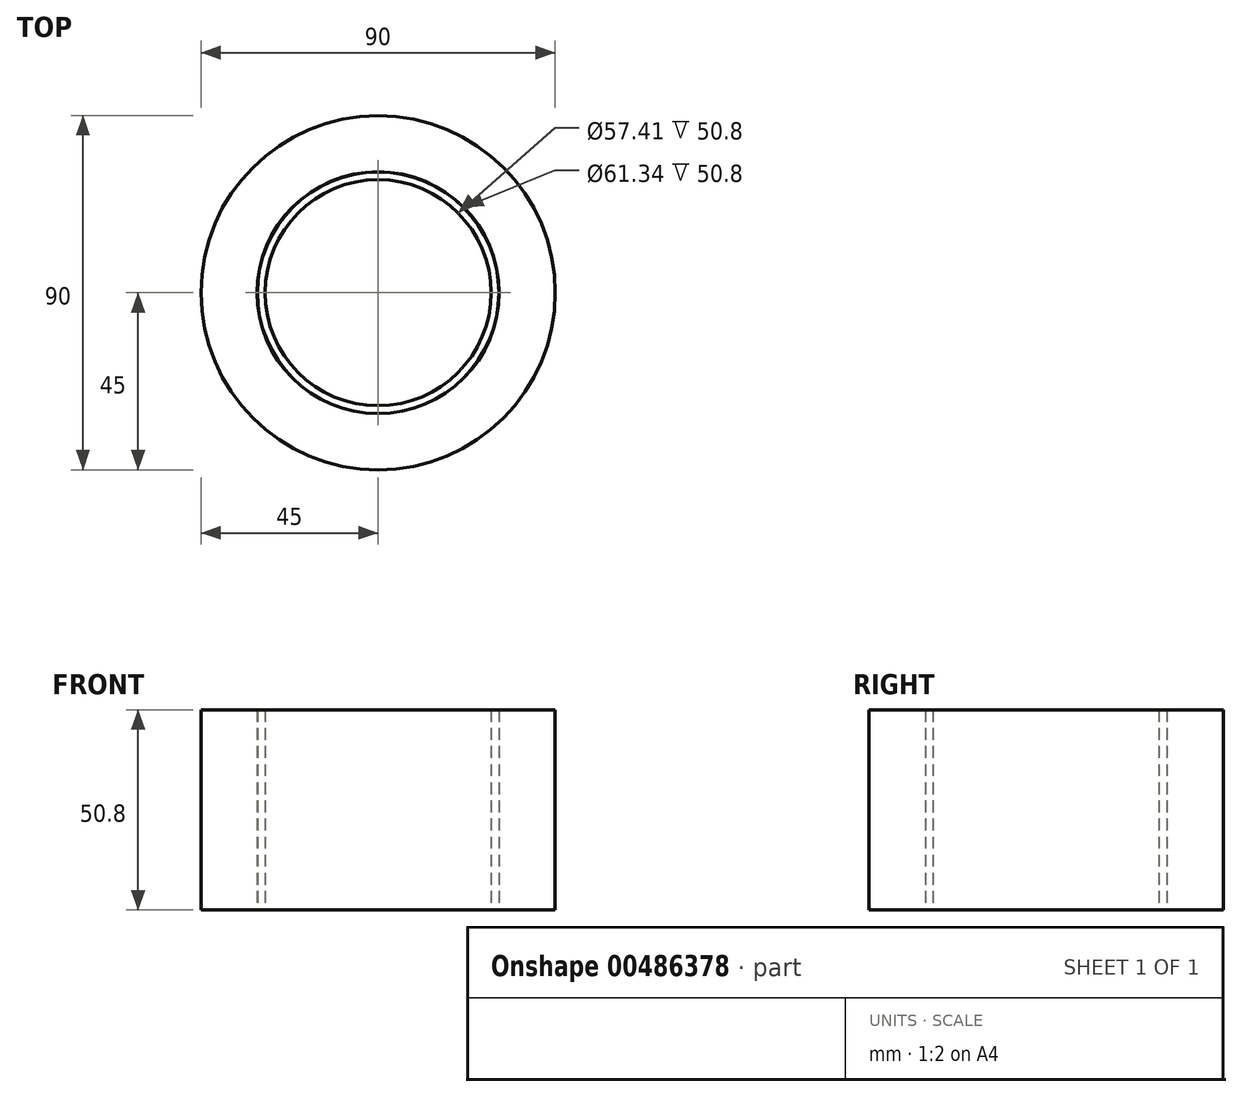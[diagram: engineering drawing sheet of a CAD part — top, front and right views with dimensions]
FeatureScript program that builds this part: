
annotation { "Feature Type Name" : "Feature", "Feature Type Description" : "" }
export const myFeature = defineFeature(function(context is Context, id is Id, definition is map)
    precondition{}
    {
        {
            var Q0;
            Q0=qCreatedBy(makeId("Top.planeOp"),FACE);
            var sketch = newSketch(context, id + "F0", { "sketchPlane" : qUnion([Q0])});
            skCircle(sketch, "E0", {"center": v(0, 0) * mm, "radius": 45 * mm});
            skCircle(sketch, "E1", {"center": v(0, 0) * mm, "radius": 30.67 * mm});
            skSolve(sketch);
        }
        {
            var Q0;
            Q0 = qSketchRegion(id + "F0", true);
            extrude(context, id + "F1", {"entities" : qUnion([Q0]), "depth" : 25.4 * mm});
        }
        {
            var Q0;
            Q0=makeQuery(id+"F1.opExtrude","CAP_FACE",FACE,{"disambiguationData":[OSD([sQuery(id+"F0.wireOp",EDGE,"E0"),sQuery(id+"F0.wireOp",EDGE,"E1")])],"isStart":false});
            extrude(context, id + "F2", {"entities" : qUnion([Q0]), "operationType" : NewBodyOperationType.ADD, "depth" : 25.4 * mm});
        }
        {
            var Q0;
            Q0=qCreatedBy(makeId("Top.planeOp"),FACE);
            var sketch = newSketch(context, id + "F3", { "sketchPlane" : qUnion([Q0])});
            skCircle(sketch, "E2", {"center": v(0, 0) * mm, "radius": 30.72 * mm});
            skCircle(sketch, "E3", {"center": v(0, 0) * mm, "radius": 28.7 * mm});
            skSolve(sketch);
        }
        {
            var Q0;
            Q0 = qSketchRegion(id + "F3", true);
            extrude(context, id + "F4", {"entities" : qUnion([Q0]), "depth" : 50.8 * mm});
        }
    });
